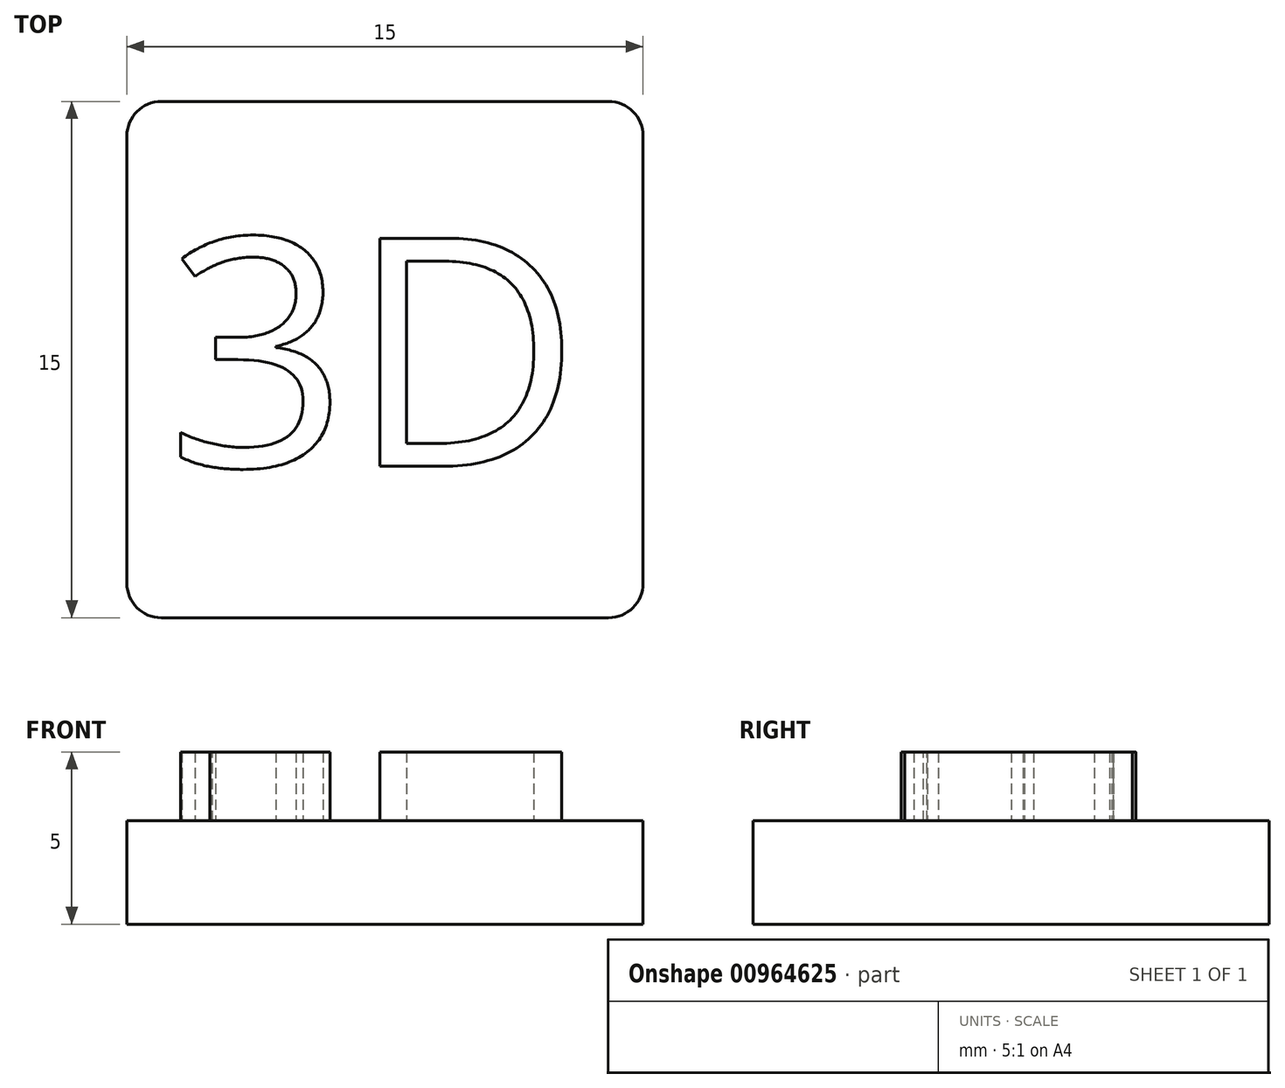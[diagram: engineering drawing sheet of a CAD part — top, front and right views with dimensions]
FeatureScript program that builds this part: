
annotation { "Feature Type Name" : "Feature", "Feature Type Description" : "" }
export const myFeature = defineFeature(function(context is Context, id is Id, definition is map)
    precondition{}
    {
        {
            var Q0;
            Q0=qCreatedBy(makeId("Top.planeOp"),FACE);
            var sketch = newSketch(context, id + "F0", { "sketchPlane" : qUnion([Q0])});
            skLineSegment(sketch, "E0.bottom", {"start": v(6.5, -7.5) * mm, "end": v(-6.5, -7.5) * mm});
            skLineSegment(sketch, "E0.top", {"start": v(6.5, 7.5) * mm, "end": v(-6.5, 7.5) * mm});
            skLineSegment(sketch, "E0.left", {"start": v(7.5, -6.5) * mm, "end": v(7.5, 6.5) * mm});
            skLineSegment(sketch, "E0.right", {"start": v(-7.5, -6.5) * mm, "end": v(-7.5, 6.5) * mm});
            skPoint(sketch, "E0.middle", {"position": v(0, 0) * mm});
            skPoint(sketch, "E1.visualSharp", {"position": v(-7.5, 7.5) * mm});
            skArc(sketch, "E1.filletArc", {"start": v(-6.5, 7.5) * mm, "mid": v(-7.2, 7.2) * mm, "end": v(-7.5, 6.5) * mm});
            skPoint(sketch, "E2.visualSharp", {"position": v(-7.5, -7.5) * mm});
            skArc(sketch, "E2.filletArc", {"start": v(-7.5, -6.5) * mm, "mid": v(-7.2, -7.2) * mm, "end": v(-6.5, -7.5) * mm});
            skPoint(sketch, "E3.visualSharp", {"position": v(7.5, -7.5) * mm});
            skArc(sketch, "E3.filletArc", {"start": v(6.5, -7.5) * mm, "mid": v(7.2, -7.2) * mm, "end": v(7.5, -6.5) * mm});
            skPoint(sketch, "E4.visualSharp", {"position": v(7.5, 7.5) * mm});
            skArc(sketch, "E4.filletArc", {"start": v(7.5, 6.5) * mm, "mid": v(7.2, 7.2) * mm, "end": v(6.5, 7.5) * mm});
            skSolve(sketch);
        }
        {
            var Q0;
            Q0 = qSketchRegion(id + "F0", true);
            extrude(context, id + "F1", {"entities" : qUnion([Q0]), "depth" : 3 * mm, "offsetDistance" : 25 * mm});
        }
        {
            var Q0;
            Q0=makeQuery(id+"F1.opExtrude","CAP_FACE",FACE,{"disambiguationData":[OSD([sQuery(id+"F0.wireOp",EDGE,"E0.bottom"),sQuery(id+"F0.wireOp",EDGE,"E0.top"),sQuery(id+"F0.wireOp",EDGE,"E0.left"),sQuery(id+"F0.wireOp",EDGE,"E0.right"),sQuery(id+"F0.wireOp",EDGE,"E1.filletArc"),sQuery(id+"F0.wireOp",EDGE,"E2.filletArc"),sQuery(id+"F0.wireOp",EDGE,"E3.filletArc"),sQuery(id+"F0.wireOp",EDGE,"E4.filletArc")])],"isStart":false});
            var sketch = newSketch(context, id + "F2", { "sketchPlane" : qUnion([Q0])});
            skText(sketch, "E5", { "text": "3D", "fontName": "OpenSans-Regular.ttf"});
            const initialGuessF2  = {"E5": [-0.00636, -0.0031, 1, 0, 0.00668]};
            skSetInitialGuess(sketch, initialGuessF2);
            skSolve(sketch);
        }
        {
            var Q0;
            Q0 = qSketchRegion(id + "F2", true);
            extrude(context, id + "F3", {"entities" : qUnion([Q0]), "operationType" : NewBodyOperationType.ADD, "depth" : 2 * mm, "offsetDistance" : 25 * mm});
        }
    });
